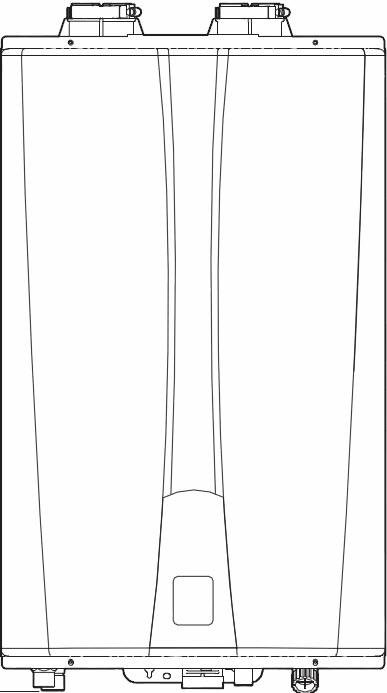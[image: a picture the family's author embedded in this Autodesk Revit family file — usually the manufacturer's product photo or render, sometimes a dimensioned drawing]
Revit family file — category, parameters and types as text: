
# Revit family: Water_Heater-Navien-NPE_A_Series
name_source: partatom
category: Mechanical Equipment
revit_build: Autodesk Revit MEP 2013 (Build: 20130531_2115(x64)
units: mm (PartAtom-declared; Revit-internal decimal feet)

## types (3) — shared parameters
Apparent Load = 0 VA
Cold Water Inlet = 1"
Default Elevation = 4' - 0"
Description = Premium Condensing Tankless Gas Water Heater (NPE-A)
Exhaust = 3"
Finish = Metal - Navien - White
Frequency = 60 Hz
Gas Inlet = 1"
Height = 2' - 3 13/32"
Hot Water Outlet = 1"
Intake = 3"
Length = 1' - 1 3/16"
Manufacturer = Navien
Natural Gas Supply Pressure = 3.5 inches - 10.5 inches
Number of Poles = 1
Phase = 1
Power Factor = 1
Product Documentation Link = http://us.navien.com
Product Name = NPE-A
Product Page URL = http://us.navien.com
Propane Gas Supply Pressure = 8.0 inches - 13.0 inches
Recirculation Inlet = 1"
URL = http://us.navien.com
Voltage = 120 V
Water Pressure = 15-150 PSI
Width = 1' - 5 5/16"

## per-type parameters (varying)
| type | Flow Rate | Heating Capacity | Model | Operating Weight |
| NPE 180A | 6.5 GPM | 150000.0 Btu/h | NPE-180A | 75.00 lb |
| NPE 210A | 10.1 GPM | 180000.0 Btu/h | NPE-210A | 82.00 lb |
| NPE 240A | 11.2 GPM | 199900.0 Btu/h | NPE-240A | 82.00 lb |

## geometry (parser evidence)
native form markers: Blend x4, Sweep x8
no freeform markers — native parametric forms only
